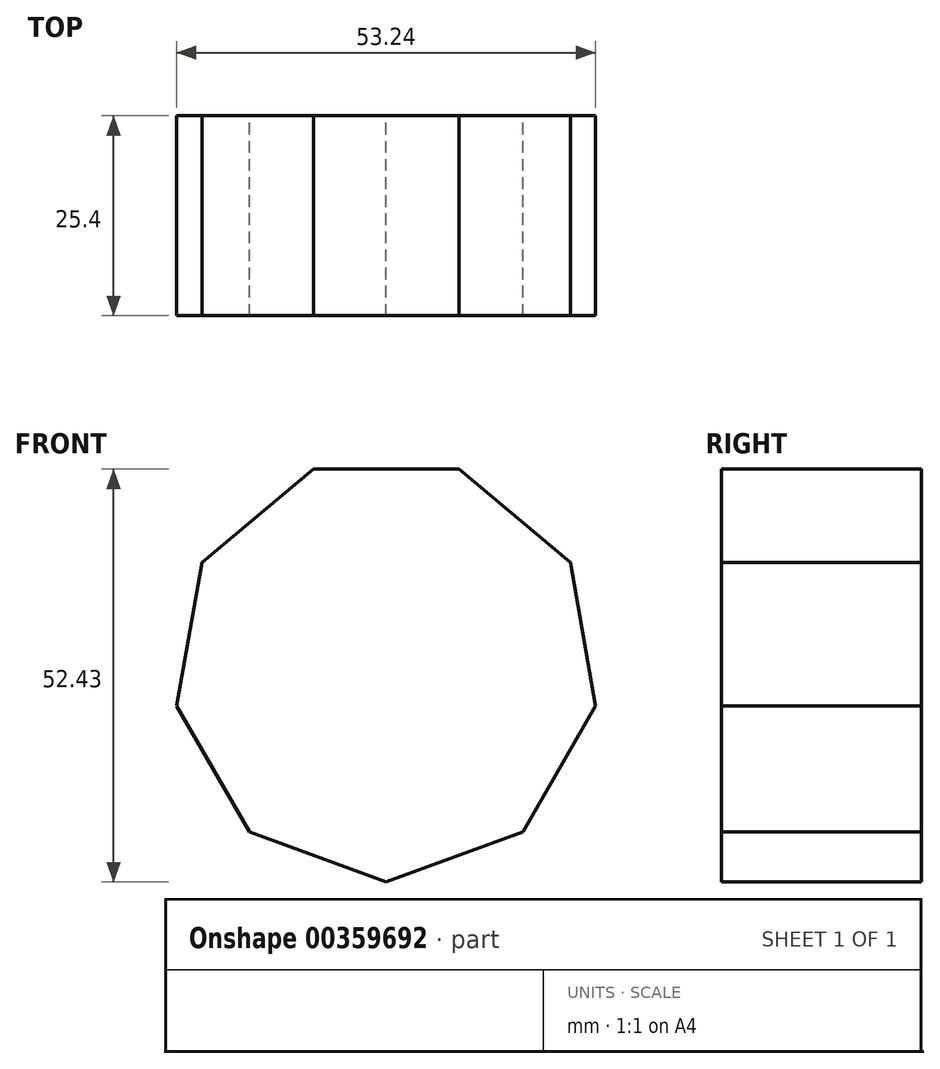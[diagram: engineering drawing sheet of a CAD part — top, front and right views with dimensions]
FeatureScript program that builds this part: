
annotation { "Feature Type Name" : "Feature", "Feature Type Description" : "" }
export const myFeature = defineFeature(function(context is Context, id is Id, definition is map)
    precondition{}
    {
        {
            var Q0;
            Q0=qCreatedBy(makeId("Front.planeOp"),FACE);
            var sketch = newSketch(context, id + "F0", { "sketchPlane" : qUnion([Q0])});
            skLineSegment(sketch, "E0", {"start": v(0, 0) * mm, "end": v(0, 25.4) * mm});
            skCircle(sketch, "E1.cCircle", {"center": v(0, 0) * mm, "radius": 25.4 * mm, "construction": true});
            skLineSegment(sketch, "E1.0", {"start": v(-9.24, 25.4) * mm, "end": v(9.24, 25.4) * mm});
            skLineSegment(sketch, "E1.1", {"start": v(9.24, 25.4) * mm, "end": v(23.4, 13.52) * mm});
            skLineSegment(sketch, "E1.2", {"start": v(23.4, 13.52) * mm, "end": v(26.62, -4.7) * mm});
            skLineSegment(sketch, "E1.3", {"start": v(26.62, -4.7) * mm, "end": v(17.37, -20.7) * mm});
            skLineSegment(sketch, "E1.4", {"start": v(17.37, -20.7) * mm, "end": v(0, -27.03) * mm});
            skLineSegment(sketch, "E1.5", {"start": v(0, -27.03) * mm, "end": v(-17.37, -20.7) * mm});
            skLineSegment(sketch, "E1.6", {"start": v(-17.37, -20.7) * mm, "end": v(-26.62, -4.7) * mm});
            skLineSegment(sketch, "E1.7", {"start": v(-26.62, -4.7) * mm, "end": v(-23.4, 13.52) * mm});
            skLineSegment(sketch, "E1.8", {"start": v(-23.4, 13.52) * mm, "end": v(-9.24, 25.4) * mm});
            skPoint(sketch, "E1.0.midPoint", {"position": v(0, 25.4) * mm});
            skSolve(sketch);
        }
        {
            var Q0;
            {var subQ0=sQuery(id+"F0.wireOp",EDGE,"E1.1");Q0=makeQuery(id+"F0.imprint","IMPRINT",FACE,{"disambiguationData":[TD([[makeQuery(id+"F0.imprint","IMPRINT",EDGE,{"derivedFrom":subQ0}),-1.0]])]});}
            extrude(context, id + "F1", {"entities" : qUnion([Q0]), "depth" : 25.4 * mm});
        }
    });
